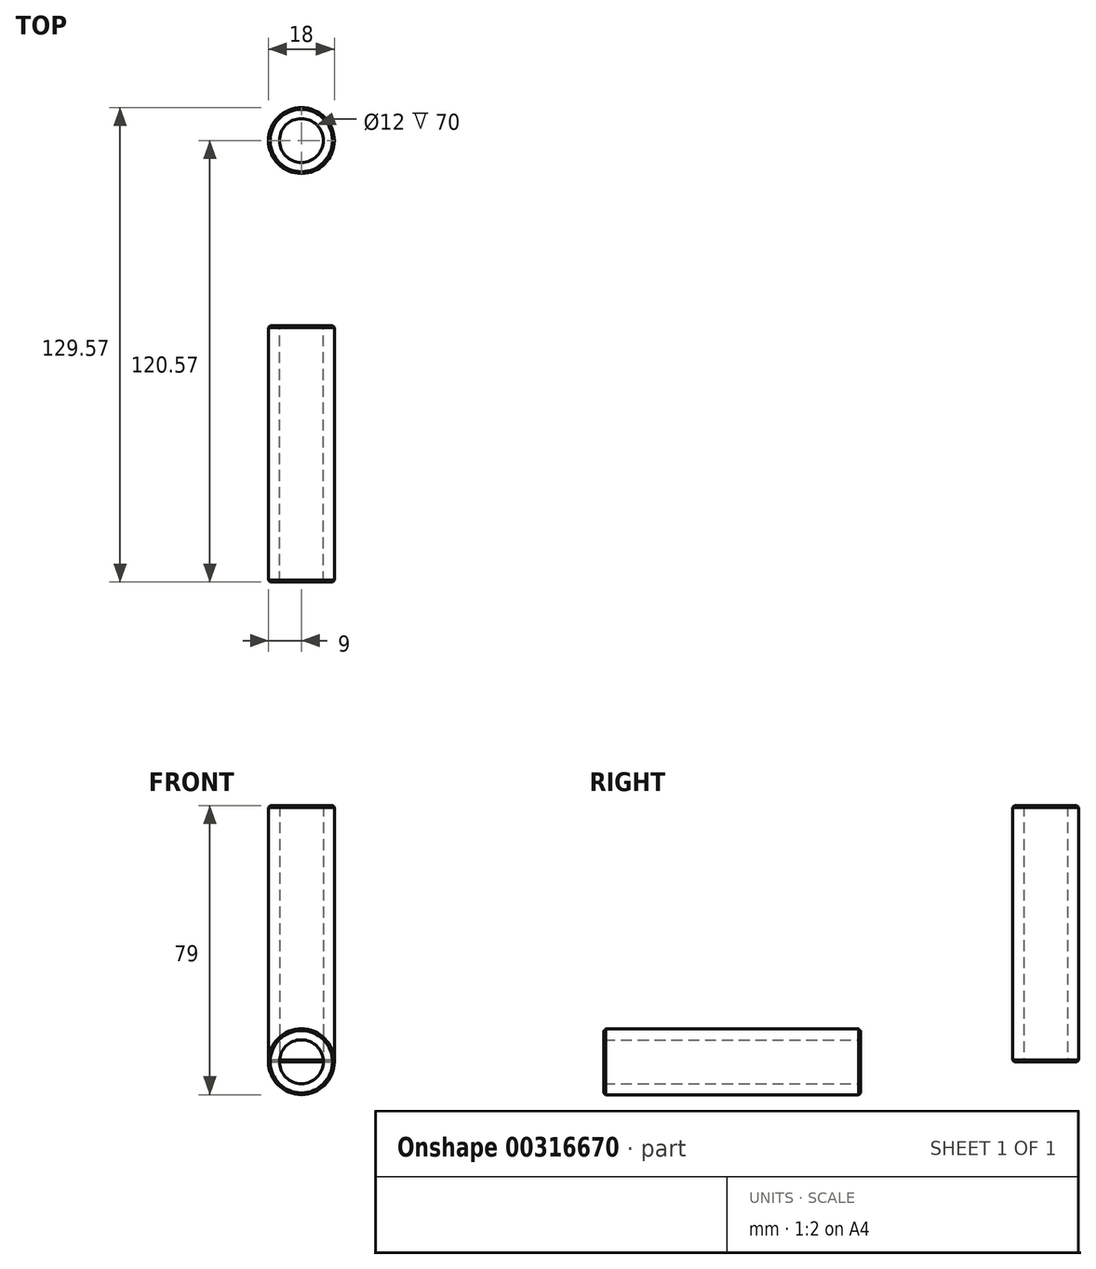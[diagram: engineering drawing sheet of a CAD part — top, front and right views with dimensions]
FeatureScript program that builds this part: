
annotation { "Feature Type Name" : "Feature", "Feature Type Description" : "" }
export const myFeature = defineFeature(function(context is Context, id is Id, definition is map)
    precondition{}
    {
        {
            assignVariable(context, id + "F0", {"name" : "Length", "anyValue" : 70});
        }
        {
            assignVariable(context, id + "F1", {"name" : "Chamfer", "anyValue" : 0.5});
        }
        {
            var Q0;
            Q0=qCreatedBy(makeId("Top.planeOp"),FACE);
            var sketch = newSketch(context, id + "F2", { "sketchPlane" : qUnion([Q0])});
            skCircle(sketch, "E0", {"center": v(0, 0) * mm, "radius": 9 * mm});
            skCircle(sketch, "E1", {"center": v(0, 0) * mm, "radius": 6 * mm});
            skSolve(sketch);
        }
        {
            var Q0;
            Q0=makeQuery(id+"F2.imprint","IMPRINT",FACE,{"disambiguationData":[TD([[makeQuery(id+"F2.imprint","IMPRINT",EDGE,{"derivedFrom":sQuery(id+"F2.wireOp",EDGE,"E0")}),1.0]])]});
            extrude(context, id + "F3", {"entities" : qUnion([Q0]), "depth" : (getVariable(context, 'Length')) * mm});
        }
        {
            var Q0;
            Q0=makeQuery(id+"F3.opExtrude","CAP_EDGE",EDGE,{"disambiguationData":[OSD([sQuery(id+"F2.wireOp",EDGE,"E0")])],"isStart":false});
            var Q1;
            Q1=makeQuery(id+"F3.opExtrude","CAP_EDGE",EDGE,{"disambiguationData":[OSD([sQuery(id+"F2.wireOp",EDGE,"E0")])],"isStart":true});
            chamfer(context, id + "F4", {"entities" : qUnion([Q0, Q1]), "width" : 0.5 * mm, "tangentPropagation" : true});
        }
        {
            var Q0;
            Q0=qCreatedBy(makeId("Right.planeOp"),FACE);
            var sketch = newSketch(context, id + "F5", { "sketchPlane" : qUnion([Q0])});
            skLineSegment(sketch, "E2", {"start": v(-50.57, 0) * mm, "end": v(-120.57, 0) * mm, "construction": true});
            skLineSegment(sketch, "E3.bottom", {"start": v(-120.57, -6) * mm, "end": v(-50.57, -6) * mm});
            skLineSegment(sketch, "E3.top", {"start": v(-120.57, -9) * mm, "end": v(-50.57, -9) * mm});
            skLineSegment(sketch, "E3.left", {"start": v(-120.57, -6) * mm, "end": v(-120.57, -9) * mm});
            skLineSegment(sketch, "E3.right", {"start": v(-50.57, -6) * mm, "end": v(-50.57, -9) * mm});
            skSolve(sketch);
        }
        {
            var Q0;
            Q0=makeQuery(id+"F5.imprint","IMPRINT",FACE,{"disambiguationData":[TD([[makeQuery(id+"F5.imprint","IMPRINT",EDGE,{"derivedFrom":sQuery(id+"F5.wireOp",EDGE,"E3.bottom")}),-1.0]])]});
            var Q1;
            Q1=sQuery(id+"F5.wireOp",EDGE,"E2");
            revolve(context, id + "F6", {"entities" : qUnion([Q0]), "axis" : qUnion([Q1]), "revolveType" : RevolveType.FULL});
        }
        {
            var Q0;
            Q0=makeQuery(id+"F6.opRevolve","SWEPT_EDGE",EDGE,{"disambiguationData":[OSD([sQuery(id+"F5.wireOp",EDGE,"E3.top"),sQuery(id+"F5.wireOp",EDGE,"E3.left")])]});
            var Q1;
            Q1=makeQuery(id+"F6.opRevolve","SWEPT_EDGE",EDGE,{"disambiguationData":[OSD([sQuery(id+"F5.wireOp",EDGE,"E3.top"),sQuery(id+"F5.wireOp",EDGE,"E3.right")])]});
            chamfer(context, id + "F7", {"entities" : qUnion([Q0, Q1]), "width" : (getVariable(context, 'Chamfer')) * mm, "tangentPropagation" : true});
        }
    });
